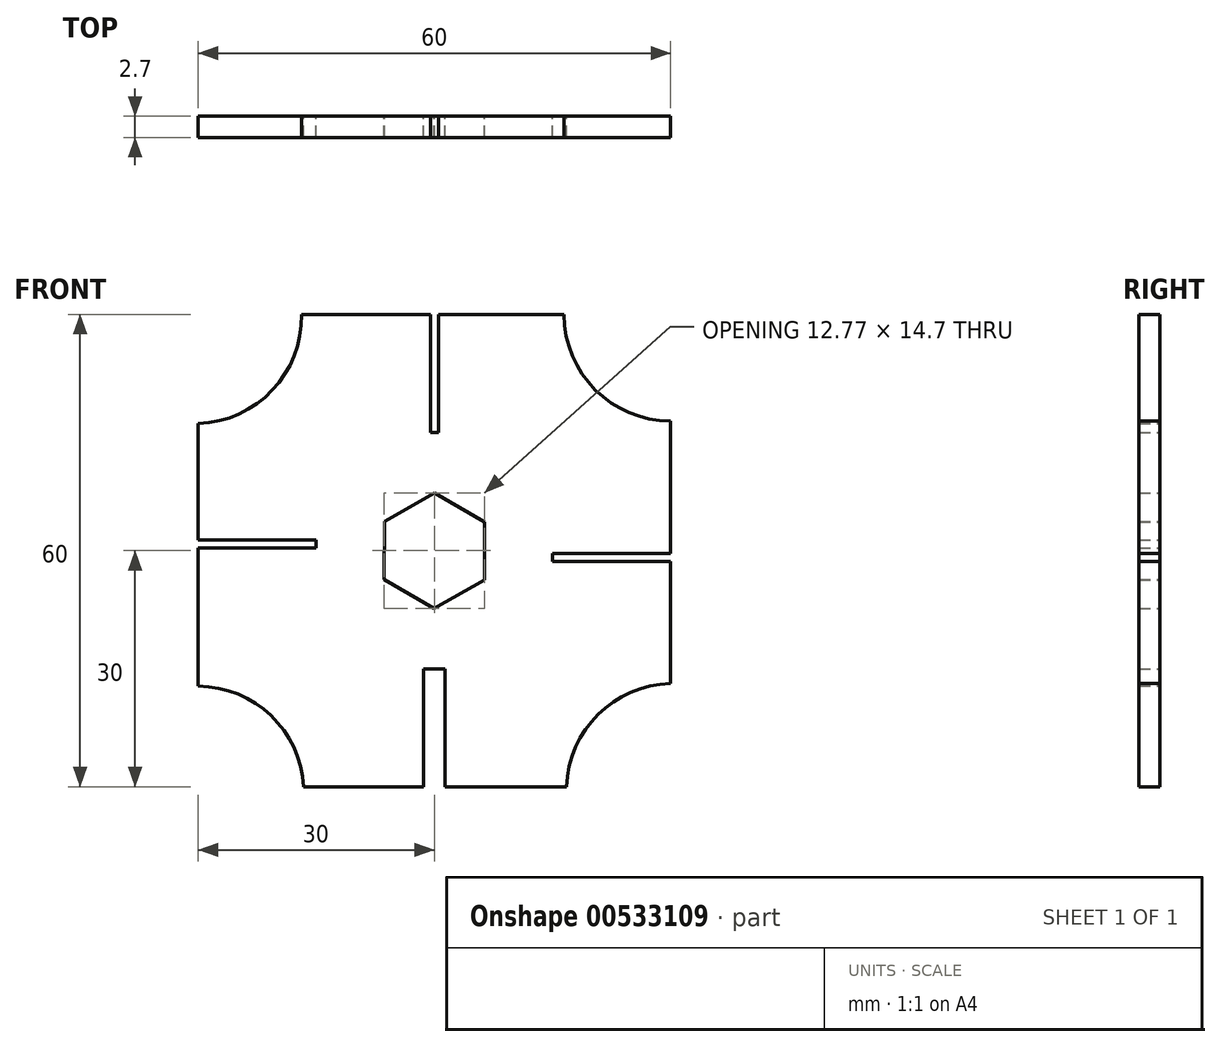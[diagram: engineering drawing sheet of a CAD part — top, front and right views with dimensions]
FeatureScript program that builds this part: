
annotation { "Feature Type Name" : "Feature", "Feature Type Description" : "" }
export const myFeature = defineFeature(function(context is Context, id is Id, definition is map)
    precondition{}
    {
        {
            var Q0;
            Q0=qCreatedBy(makeId("Front.planeOp"),FACE);
            var sketch = newSketch(context, id + "F0", { "sketchPlane" : qUnion([Q0])});
            skLineSegment(sketch, "E0.bottom", {"start": v(-16.9, 30) * mm, "end": v(-0.5, 30) * mm});
            skLineSegment(sketch, "E0.top", {"start": v(-16.6, -30) * mm, "end": v(-1.35, -30) * mm});
            skLineSegment(sketch, "E0.left", {"start": v(-30, 16.15) * mm, "end": v(-30, 1.35) * mm});
            skLineSegment(sketch, "E0.right", {"start": v(30, 16.46) * mm, "end": v(30, -0.35) * mm});
            skPoint(sketch, "E0.middle", {"position": v(0, 0) * mm});
            skLineSegment(sketch, "E1.top", {"start": v(-0.5, 15) * mm, "end": v(0.5, 15) * mm});
            skLineSegment(sketch, "E1.left", {"start": v(-0.5, 30) * mm, "end": v(-0.5, 15) * mm});
            skLineSegment(sketch, "E1.right", {"start": v(0.5, 30) * mm, "end": v(0.5, 15) * mm});
            skPoint(sketch, "E1.middle", {"position": v(0, 30) * mm});
            skLineSegment(sketch, "E2.1.1", {"start": v(-30, 1.35) * mm, "end": v(-15, 1.35) * mm});
            skLineSegment(sketch, "E2.1.2", {"start": v(-30, 0.35) * mm, "end": v(-15, 0.35) * mm});
            skLineSegment(sketch, "E2.1.3", {"start": v(-15, 0.35) * mm, "end": v(-15, 1.35) * mm});
            skLineSegment(sketch, "E2.2.1", {"start": v(-1.35, -30) * mm, "end": v(-1.35, -15) * mm});
            skLineSegment(sketch, "E2.2.2", {"start": v(1.35, -30) * mm, "end": v(1.35, -15) * mm});
            skLineSegment(sketch, "E2.2.3", {"start": v(1.35, -15) * mm, "end": v(-1.35, -15) * mm});
            skLineSegment(sketch, "E2.3.1", {"start": v(30, -1.35) * mm, "end": v(15, -1.35) * mm});
            skLineSegment(sketch, "E2.3.2", {"start": v(30, -0.35) * mm, "end": v(15, -0.35) * mm});
            skLineSegment(sketch, "E2.3.3", {"start": v(15, -0.35) * mm, "end": v(15, -1.35) * mm});
            skLineSegment(sketch, "E3.trimOffspring", {"start": v(-30, 0.35) * mm, "end": v(-30, -17.22) * mm});
            skLineSegment(sketch, "E4.trimOffspring", {"start": v(30, -1.35) * mm, "end": v(30, -16.9) * mm});
            skPoint(sketch, "E5.orphan", {"position": v(45, -0.35) * mm});
            skPoint(sketch, "E6.orphan", {"position": v(45, -1.35) * mm});
            skLineSegment(sketch, "E7.trimOffspring", {"start": v(0.5, 30) * mm, "end": v(16.46, 30) * mm});
            skPoint(sketch, "E8.orphan", {"position": v(0.5, 45) * mm});
            skPoint(sketch, "E9.orphan", {"position": v(-0.5, 45) * mm});
            skLineSegment(sketch, "E10.trimOffspring", {"start": v(1.35, -30) * mm, "end": v(16.8, -30) * mm});
            skArc(sketch, "E11", {"start": v(16.46, 30) * mm, "mid": v(20.43, 20.43) * mm, "end": v(30, 16.46) * mm});
            skArc(sketch, "E12.1.0", {"start": v(-30, 16.15) * mm, "mid": v(-20.6, 20.38) * mm, "end": v(-16.9, 30) * mm});
            skArc(sketch, "E12.2.0", {"start": v(-16.6, -30) * mm, "mid": v(-20.77, -20.95) * mm, "end": v(-30, -17.22) * mm});
            skArc(sketch, "E12.3.0", {"start": v(30, -16.9) * mm, "mid": v(20.79, -20.82) * mm, "end": v(16.8, -30) * mm});
            skPoint(sketch, "E12.center", {"position": v(-0.05, -0.38) * mm});
            skPoint(sketch, "E13.orphan", {"position": v(-30, 30) * mm});
            skPoint(sketch, "E14.orphan", {"position": v(30, -30) * mm});
            skPoint(sketch, "E15.orphan", {"position": v(-30, -30) * mm});
            skCircle(sketch, "E16.cCircle", {"center": v(0, 0) * mm, "radius": 6.37 * mm, "construction": true});
            skLineSegment(sketch, "E16.0", {"start": v(-6.35, 3.7) * mm, "end": v(0.03, 7.35) * mm});
            skLineSegment(sketch, "E16.1", {"start": v(0.03, 7.35) * mm, "end": v(6.38, 3.65) * mm});
            skLineSegment(sketch, "E16.2", {"start": v(6.38, 3.65) * mm, "end": v(6.35, -3.7) * mm});
            skLineSegment(sketch, "E16.3", {"start": v(6.35, -3.7) * mm, "end": v(-0.03, -7.35) * mm});
            skLineSegment(sketch, "E16.4", {"start": v(-0.03, -7.35) * mm, "end": v(-6.38, -3.65) * mm});
            skLineSegment(sketch, "E16.5", {"start": v(-6.38, -3.65) * mm, "end": v(-6.35, 3.7) * mm});
            skPoint(sketch, "E16.0.midPoint", {"position": v(-3.16, 5.53) * mm});
            skSolve(sketch);
        }
        {
            var Q0;
            Q0 = qSketchRegion(id + "F0", true);
            extrude(context, id + "F1", {"entities" : qUnion([Q0]), "depth" : 2.7 * mm, "offsetDistance" : 25 * mm});
        }
    });
